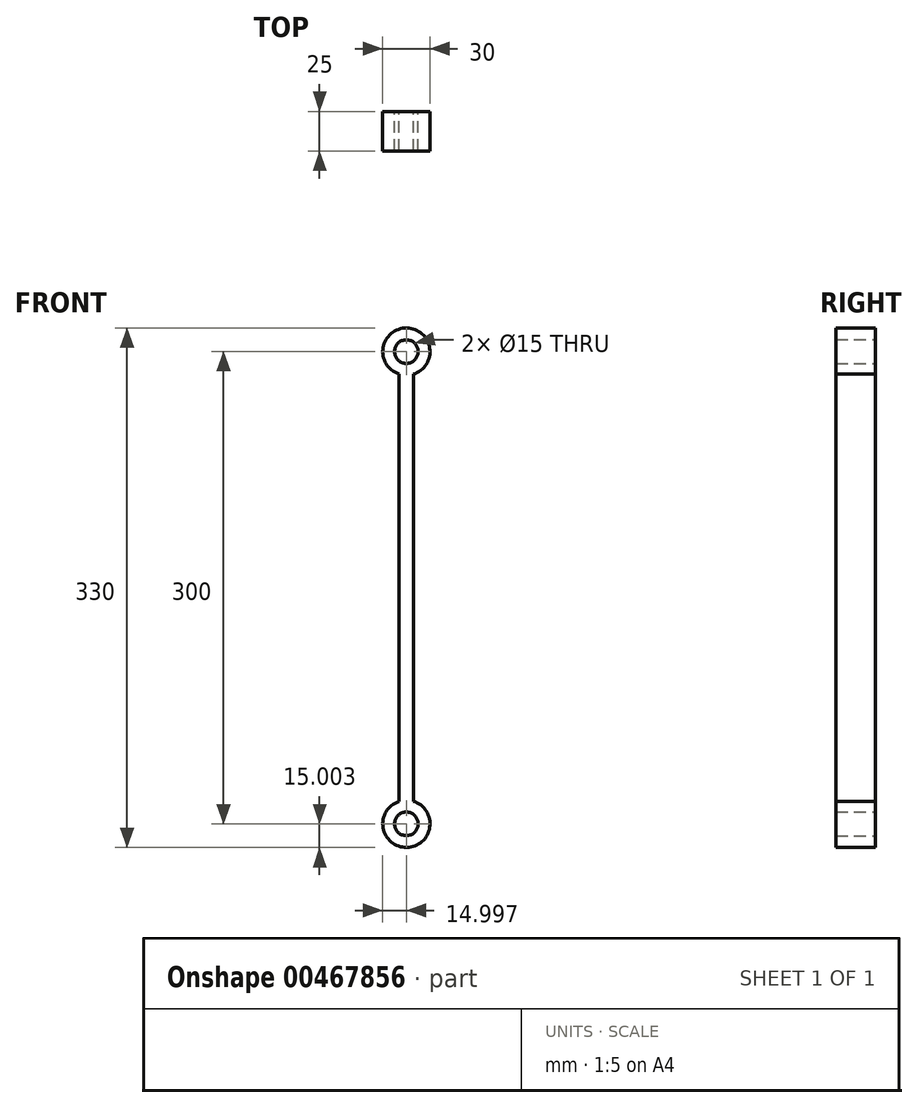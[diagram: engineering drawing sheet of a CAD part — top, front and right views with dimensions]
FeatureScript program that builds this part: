
annotation { "Feature Type Name" : "Feature", "Feature Type Description" : "" }
export const myFeature = defineFeature(function(context is Context, id is Id, definition is map)
    precondition{}
    {
        {
            var Q0;
            Q0=qCreatedBy(makeId("Front.planeOp"),FACE);
            var sketch = newSketch(context, id + "F0", { "sketchPlane" : qUnion([Q0])});
            skCircle(sketch, "E0", {"center": v(-50.94, 243.4) * mm, "radius": 15 * mm});
            skCircle(sketch, "E1", {"center": v(-50.94, 243.4) * mm, "radius": 7.5 * mm});
            skCircle(sketch, "E2", {"center": v(-50.94, -56.6) * mm, "radius": 15 * mm});
            skCircle(sketch, "E3", {"center": v(-50.94, -56.6) * mm, "radius": 7.5 * mm});
            skLineSegment(sketch, "E4", {"start": v(-55.69, 229.17) * mm, "end": v(-55.69, -42.37) * mm});
            skLineSegment(sketch, "E5", {"start": v(-46.56, 229.06) * mm, "end": v(-46.56, -42.25) * mm});
            skSolve(sketch);
        }
        {
            var Q0;
            Q0 = qSketchRegion(id + "F0", true);
            extrude(context, id + "F1", {"entities" : qUnion([Q0]), "depth" : 25 * mm});
        }
    });
